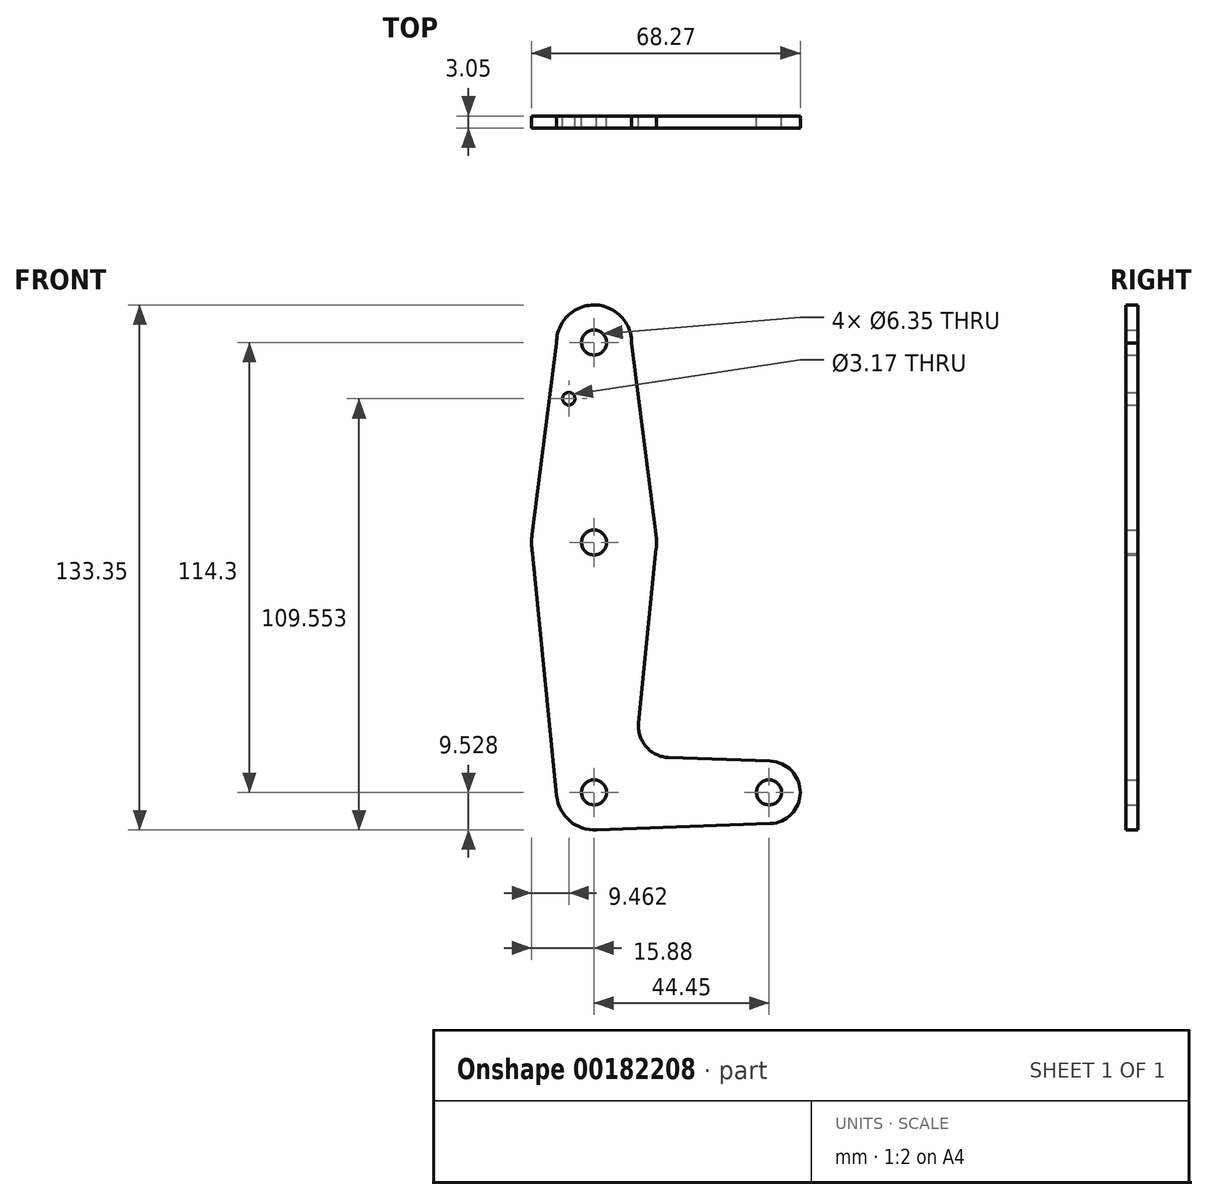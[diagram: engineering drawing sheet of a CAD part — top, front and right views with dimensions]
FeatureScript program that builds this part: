
annotation { "Feature Type Name" : "Feature", "Feature Type Description" : "" }
export const myFeature = defineFeature(function(context is Context, id is Id, definition is map)
    precondition{}
    {
        {
            var Q0;
            Q0=qCreatedBy(makeId("Front.planeOp"),FACE);
            var sketch = newSketch(context, id + "F0", { "sketchPlane" : qUnion([Q0])});
            skCircle(sketch, "E0", {"center": v(0, 93.96) * mm, "radius": 9.53 * mm});
            skCircle(sketch, "E1", {"center": v(0, 43.16) * mm, "radius": 15.88 * mm});
            skCircle(sketch, "E2", {"center": v(0, -20.34) * mm, "radius": 9.53 * mm});
            skCircle(sketch, "E3", {"center": v(44.45, -20.34) * mm, "radius": 7.94 * mm});
            skLineSegment(sketch, "E4", {"start": v(0, 93.96) * mm, "end": v(0, 43.16) * mm, "construction": true});
            skLineSegment(sketch, "E5", {"start": v(0, 43.16) * mm, "end": v(0, -20.34) * mm, "construction": true});
            skLineSegment(sketch, "E6", {"start": v(0, -20.34) * mm, "end": v(44.45, -20.34) * mm, "construction": true});
            skLineSegment(sketch, "E7", {"start": v(-9.52, 93.83) * mm, "end": v(-15.75, 45.17) * mm});
            skLineSegment(sketch, "E8", {"start": v(-15.61, 40.3) * mm, "end": v(-9.48, -21.29) * mm});
            skLineSegment(sketch, "E9", {"start": v(9.52, 93.85) * mm, "end": v(15.75, 45.17) * mm});
            skLineSegment(sketch, "E10", {"start": v(15.8, 41.57) * mm, "end": v(11.34, -2.75) * mm});
            skLineSegment(sketch, "E11", {"start": v(18.97, -11.5) * mm, "end": v(44.73, -12.4) * mm});
            skLineSegment(sketch, "E12", {"start": v(0, -29.87) * mm, "end": v(44.73, -28.27) * mm});
            skCircle(sketch, "E13", {"center": v(0, 93.96) * mm, "radius": 3.18 * mm});
            skCircle(sketch, "E14", {"center": v(0, 43.16) * mm, "radius": 3.18 * mm});
            skCircle(sketch, "E15", {"center": v(0, -20.34) * mm, "radius": 3.18 * mm});
            skCircle(sketch, "E16", {"center": v(44.45, -20.34) * mm, "radius": 3.18 * mm});
            skCircle(sketch, "E17", {"center": v(-6.42, 79.68) * mm, "radius": 1.59 * mm});
            skPoint(sketch, "E18.centerSnap0", {"position": v(12.68, 10.61) * mm});
            skPoint(sketch, "E19.newPointA", {"position": v(9.57, -20.34) * mm});
            skArc(sketch, "E19.filletArc", {"start": v(11.34, -2.75) * mm, "mid": v(13.26, -8.77) * mm, "end": v(18.97, -11.5) * mm});
            skSolve(sketch);
        }
        {
            var Q0;
            Q0 = qSketchRegion(id + "F0", true);
            extrude(context, id + "F1", {"entities" : qUnion([Q0]), "depth" : 3.05 * mm});
        }
    });
